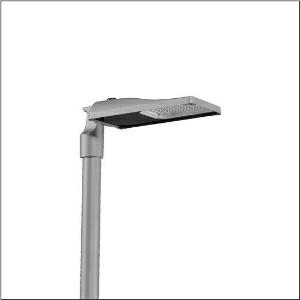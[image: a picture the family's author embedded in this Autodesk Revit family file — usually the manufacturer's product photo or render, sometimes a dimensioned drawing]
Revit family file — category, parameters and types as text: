
# Revit family: streetlight_sl_31_mini___st1_0a_5xh6d3as08ha_e0b1
name_source: partatom
category: Lighting Fixtures
units: mm (PartAtom-declared; Revit-internal decimal feet)

## family parameters
Cut with Voids When Loaded = No
Host = Face
Light Source = No
Part Type = Normal
Room Calculation Point = No
Round Connector Dimension = Use Diameter
Shared = No

## types (1)
- --- (1 x LED, 9230 lm, 68.3 W, 3000K)
    Apparent Load = 68 VA
    CIE Flux Codes = 37 72 97 100 100
    Color Rendering = 70
    Color Temperature = 3000K
    Default Elevation = 1800 mm
    Description = Streetlight SL 31 mini D4i mast luminaire for post-top, side-entry; light control with lens of PMMA; light distribution: ST1.0a, direct asymmetric distribution, for standard-compliant lighting for roads and squares; LED: luminous flux: 9.230lm, light colour: 730, colour temperature: 3000K; luminous efficacy: 135,1lm/W; control: pre-setting: logarithmic dimming characteristic, flexible luminous flux parameterisation, time-dependent luminous flux control, constant luminous flux control, power reduction, intelligent temperature release in ECG and LED module, overheat protection; luminaire housing, of diecast aluminium, Siteco® metallic grey (DB 702S), corrosivity category C5 high according to DIN EN ISO 12944; cover of toughened safety glass, transparent, opened without tools; mast flange of diecast aluminium, Siteco® metallic grey (DB 702S), spigot size: 76/60mm, mast flange included unmounted; with cable H07RN-F 2x 1.5mm², cable length: 8,5m, connection cable pre-assembled; mains connection: 220..240V, AC, 50/60Hz; power consumption (at start of service life): 68,3W / (at end of service life): 74,5W / (with reduced operation 50%): 29,5W; protection rating (complete): IP66; insulation class (complete): insulation class II (safety insulation); impact resistance: IK10; certification: CE, ENEC, ENEC+, VDE, UKCA, ZD4i; permissible operating ambient temperature for outdoor applications: -40..+50°C; packaging unit: 1 piece

Light Distribution: ST1.0a
    Height = 76 mm
    Lamp = 1 x LED
    Lamp Light Flux = 9230 lm
    Lamp Power = 68.3 W
    Lamp count = 1
    Length = 547 mm
    Luminous efficacy = 135 lm/W
    Manufacturer = Siteco
    ModVariant = No
    Model = 5XH6D3AS08HA
    Number of Poles = 1
    OnlyDefault = Yes
    Power Factor = 1
    Product Name = Streetlight SL 31 mini | ST1.0a
    Product group = mast luminaire | pylon top
    ProductGroupID = 6100
    Protection Class = Protection class II
    Protection Degree = IP 66
    RLX_Detail_Level = 1
    RLX_Emergency_Light_Flux = 0 lm
    RLX_Emergency_Type = 0
    RLX_Emergency_Type_DB = No
    RlxData = <blob elided: 24257 chars, md5=3608e4e7>
    Socket = socket
    Standby Power = 0 W
    System Light Flux = 9230 lm
    System Power = 68 W
    Type Comments = factory setting: luminous flux: 100 % | dim-lin: 254 | 692 mA
    Type Image = l_1300330.jpg
    URL = http://relux.com
    VarID = @adj_001945
    Voltage = 0 V
    Weight = 0.00 kg
    Width = 265 mm

## geometry (parser evidence)
native form markers: Blend x4, Sweep x11
no freeform markers — native parametric forms only
